# Revit family: xxx4-xxx-xx-xx-840K
name_source: partatom
category: Lighting Fixtures
units: mm (PartAtom-declared; Revit-internal decimal feet)

## family parameters
Always vertical = Yes
Cut with Voids When Loaded = No
Host = Ceiling
Light Source = Yes
OmniClass Number = 23.80.70.11
OmniClass Title = Luminaries for Internal Lighting
Part Type = Normal
Room Calculation Point = No
Round Connector Dimension = Use Diameter
Shared = No

## types (43) — shared parameters
Assembly Code = D5020200
Color Filter = 16777215
Description = Click image to enlarge
LED Troffer Dish Circular Recessed
Dimming Lamp Color Temperature Shift = <None>
Emit Shape Visible in Rendering = No
Emit from Circle Diameter = 2' - 0"
Housing Finish = Metal - Viscor - White
Lamp = LED
Length = 1' - 7 5/8"
Lens Finish = Polycarbonate - Viscor - Frosted Round
Manufacturer = CERTOLUX A DIVISION OF VISCOR
Model = LTDCR
Tilt Angle = 90.00°
URL = https://www.viscor.com
Voltage = 120 V
Width = 0' - 9 3/8"

## per-type parameters (varying)
| type | Apparent Load | Lamp Wattage | Photometric Web File |
| xxx4-FSL-SS-MED-840K035LUNV | 36 VA | 36 VA | xxx4-FSL-SS-MED-840K035LUNV.ies |
| xxx4-FSL-SS-MED-840K045LUNV | 46 VA | 46 VA | xxx4-FSL-SS-MED-840K045LUNV.ies |
| xxx4-FSL-SS-WD-840K035LUNV | 36 VA | 36 VA | xxx4-FSL-SS-WD-840K035LUNV.ies |
| xxx4-FSL-SS-WD-840K045LUNV | 46 VA | 46 VA | xxx4-FSL-SS-WD-840K045LUNV.ies |
| xxx4-RSL-PL-WD-840K020LUNV | 21 VA | 21 VA | xxx4-RSL-PL-WD-840K020LUNV.ies |
| xxx4-RSL-PL-WD-840K030LUNV | 31 VA | 31 VA | xxx4-RSL-PL-WD-840K030LUNV.ies |
| xxx4-RSL-PL-WD-840K035LUNV | 36 VA | 36 VA | xxx4-RSL-PL-WD-840K035LUNV.ies |
| xxx4-RSL-PL-WD-840K040LUNV | 41 VA | 41 VA | xxx4-RSL-PL-WD-840K040LUNV.ies |
| xxx4-RSL-PL-WD-840K050LUNV | 51 VA | 51 VA | xxx4-RSL-PL-WD-840K050LUNV.ies |
| xxx4-RSL-SS-MED-840K035LUNV | 36 VA | 36 VA | xxx4-RSL-SS-MED-840K035LUNV.ies |
| xxx4-RSL-SS-MED-840K045LUNV | 46 VA | 46 VA | xxx4-RSL-SS-MED-840K045LUNV.ies |
| xxx4-RSL-SS-WD-840K035LUNV | 36 VA | 36 VA | xxx4-RSL-SS-WD-840K035LUNV.ies |
| xxx4-RSL-SS-WD-840K045LUNV | 46 VA | 46 VA | xxx4-RSL-SS-WD-840K045LUNV.ies |
| xxx6-FSL-MW-WD-840K020LUNV | 21 VA | 21 VA | xxx6-FSL-MW-WD-840K020LUNV.ies |
| xxx6-FSL-MW-WD-840K030LUNV | 31 VA | 31 VA | xxx6-FSL-MW-WD-840K030LUNV.ies |
| xxx6-FSL-MW-WD-840K035LUNV | 36 VA | 36 VA | xxx6-FSL-MW-WD-840K035LUNV.ies |
| xxx6-FSL-MW-WD-840K040LUNV | 41 VA | 41 VA | xxx6-FSL-MW-WD-840K040LUNV.ies |
| xxx6-FSL-MW-WD-840K045LUNV | 46 VA | 46 VA | xxx6-FSL-MW-WD-840K045LUNV.ies |
| xxx6-FSL-MW-WD-840K050LUNV | 51 VA | 51 VA | xxx6-FSL-MW-WD-840K050LUNV.ies |
| xxx6-FSL-PL-WD-840K020LUNV | 21 VA | 21 VA | xxx6-FSL-PL-WD-840K020LUNV.ies |
| xxx6-FSL-PL-WD-840K030LUNV | 31 VA | 31 VA | xxx6-FSL-PL-WD-840K030LUNV.ies |
| xxx6-FSL-PL-WD-840K035LUNV | 36 VA | 36 VA | xxx6-FSL-PL-WD-840K035LUNV.ies |
| xxx6-FSL-PL-WD-840K040LUNV | 41 VA | 41 VA | xxx6-FSL-PL-WD-840K040LUNV.ies |
| xxx6-FSL-PL-WD-840K045LUNV | 46 VA | 46 VA | xxx6-FSL-PL-WD-840K045LUNV.ies |
| xxx6-FSL-PL-WD-840K050LUNV | 51 VA | 51 VA | xxx6-FSL-PL-WD-840K050LUNV.ies |
| xxx6-RSL-MW-WD-840K020LUNV | 21 VA | 21 VA | xxx6-RSL-MW-WD-840K020LUNV.ies |
| xxx6-RSL-MW-WD-840K030LUNV | 31 VA | 31 VA | xxx6-RSL-MW-WD-840K030LUNV.ies |
| xxx6-RSL-MW-WD-840K035LUNV | 36 VA | 36 VA | xxx6-RSL-MW-WD-840K035LUNV.ies |
| xxx6-RSL-MW-WD-840K040LUNV | 41 VA | 41 VA | xxx6-RSL-MW-WD-840K040LUNV.ies |
| xxx6-RSL-MW-WD-840K045LUNV | 46 VA | 46 VA | xxx6-RSL-MW-WD-840K045LUNV.ies |
| xxx6-RSL-MW-WD-840K050LUNV | 51 VA | 51 VA | xxx6-RSL-MW-WD-840K050LUNV.ies |
| xxx6-RSL-PL-WD-840K020LUNV | 21 VA | 21 VA | xxx6-RSL-PL-WD-840K020LUNV.ies |
| xxx6-RSL-PL-WD-840K030LUNV | 31 VA | 31 VA | xxx6-RSL-PL-WD-840K030LUNV.ies |
| xxx6-RSL-PL-WD-840K035LUNV | 36 VA | 36 VA | xxx6-RSL-PL-WD-840K035LUNV.ies |
| xxx6-RSL-PL-WD-840K040LUNV | 41 VA | 41 VA | xxx6-RSL-PL-WD-840K040LUNV.ies |
| xxx6-RSL-PL-WD-840K045LUNV | 46 VA | 46 VA | xxx6-RSL-PL-WD-840K045LUNV.ies |
| xxx6-RSL-PL-WD-840K050LUNV | 51 VA | 51 VA | xxx6-RSL-PL-WD-840K050LUNV.ies |
| xxx6-FSL-SS-MED-840K045LUNV | 46 VA | 46 VA | xxx6-FSL-SS-MED-840K045LUNV.ies |
| xxx6-FSL-SS-MED-840K035LUNV | 36 VA | 36 VA | xxx6-FSL-SS-MED-840K035LUNV.ies |
| xxx6-FSL-SS-MED-840K025LUNV | 26 VA | 26 VA | xxx6-FSL-SS-MED-840K025LUNV.ies |
| xxx6-RSL-SS-MED-840K035LUNV | 36 VA | 36 VA |  |
| xxx6-RSL-SS-MED-840K045LUNV | 46 VA | 46 VA | xxx6-RSL-SS-MED-840K045LUNV.ies |
| xxx6-RSL-SS-MED-840K025LUNV | 26 VA | 26 VA | xxx6-RSL-SS-MED-840K025LUNV.ies |

## geometry (parser evidence)
native form markers: Sweep x3
no freeform markers — native parametric forms only
